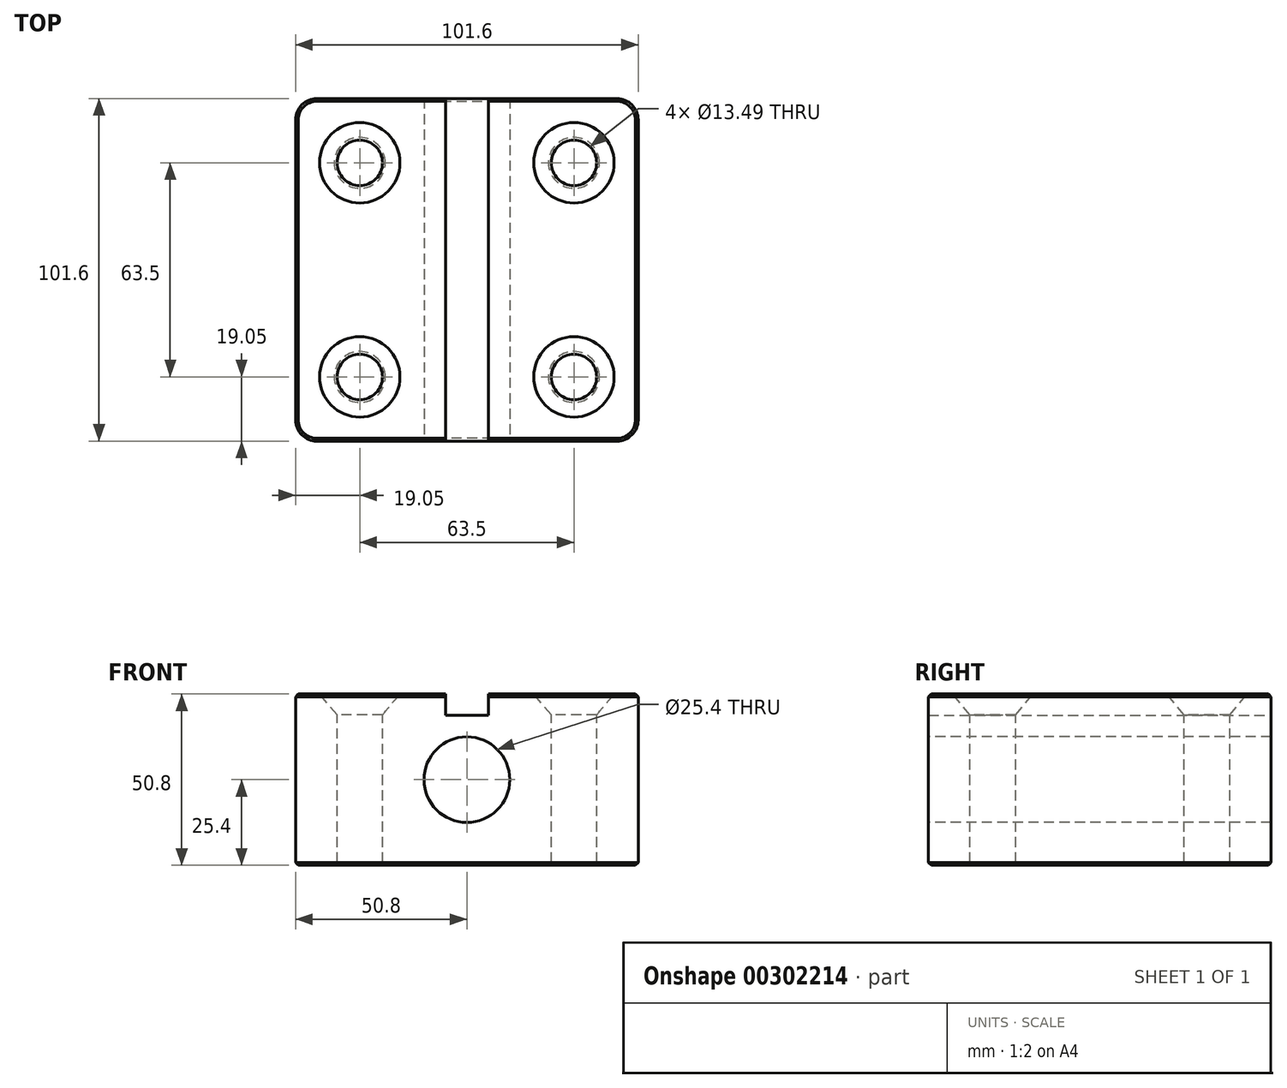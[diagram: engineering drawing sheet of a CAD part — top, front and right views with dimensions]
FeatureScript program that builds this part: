
annotation { "Feature Type Name" : "Feature", "Feature Type Description" : "" }
export const myFeature = defineFeature(function(context is Context, id is Id, definition is map)
    precondition{}
    {
        {
            var Q0;
            Q0=qCreatedBy(makeId("Front.planeOp"),FACE);
            var sketch = newSketch(context, id + "F0", { "sketchPlane" : qUnion([Q0])});
            skLineSegment(sketch, "E0.bottom", {"start": v(-50.8, 25.4) * mm, "end": v(-6.35, 25.4) * mm});
            skLineSegment(sketch, "E0.top", {"start": v(-50.8, -25.4) * mm, "end": v(50.8, -25.4) * mm});
            skLineSegment(sketch, "E0.left", {"start": v(-50.8, 25.4) * mm, "end": v(-50.8, -25.4) * mm});
            skLineSegment(sketch, "E0.right", {"start": v(50.8, 25.4) * mm, "end": v(50.8, -25.4) * mm});
            skLineSegment(sketch, "E1", {"start": v(-6.35, 25.4) * mm, "end": v(-6.35, 19.05) * mm});
            skLineSegment(sketch, "E2", {"start": v(6.35, 25.4) * mm, "end": v(6.35, 19.05) * mm});
            skLineSegment(sketch, "E3", {"start": v(-6.35, 19.05) * mm, "end": v(6.35, 19.05) * mm});
            skLineSegment(sketch, "E4.trimOffspring", {"start": v(6.35, 25.4) * mm, "end": v(50.8, 25.4) * mm});
            skSolve(sketch);
        }
        {
            var Q0;
            Q0=makeQuery(id+"F0.imprint","IMPRINT",FACE,{"disambiguationData":[TD([[makeQuery(id+"F0.imprint","IMPRINT",EDGE,{"derivedFrom":sQuery(id+"F0.wireOp",EDGE,"E0.bottom")}),-1.0]])]});
            extrude(context, id + "F1", {"entities" : qUnion([Q0]), "depth" : 50.8 * mm, "hasSecondDirection" : true, "secondDirectionOppositeDirection" : true, "secondDirectionDepth" : 50.8 * mm});
        }
        {
            var Q0;
            Q0=makeQuery(id+"F1.opExtrude","SWEPT_FACE",FACE,{"disambiguationData":[OSD([sQuery(id+"F0.wireOp",EDGE,"E0.bottom")])]});
            var sketch = newSketch(context, id + "F2", { "sketchPlane" : qUnion([Q0])});
            skPoint(sketch, "E5", {"position": v(-31.75, 31.75) * mm});
            skPoint(sketch, "E6.MirrorP", {"position": v(31.75, 31.75) * mm});
            skPoint(sketch, "E7.MirrorP", {"position": v(-31.75, -31.75) * mm});
            skPoint(sketch, "E8.MirrorP", {"position": v(31.75, -31.75) * mm});
            skSolve(sketch);
        }
        {
            var Q0;
            Q0=makeQuery(id+"F1.opExtrude","CAP_EDGE",EDGE,{"disambiguationData":[OSD([sQuery(id+"F0.wireOp",EDGE,"E0.left")])],"isStart":true});
            var Q1;
            Q1=makeQuery(id+"F1.opExtrude","CAP_EDGE",EDGE,{"disambiguationData":[OSD([sQuery(id+"F0.wireOp",EDGE,"E0.left")])],"isStart":false});
            var Q2;
            Q2=makeQuery(id+"F1.opExtrude","CAP_EDGE",EDGE,{"disambiguationData":[OSD([sQuery(id+"F0.wireOp",EDGE,"E0.right")])],"isStart":true});
            var Q3;
            Q3=makeQuery(id+"F1.opExtrude","CAP_EDGE",EDGE,{"disambiguationData":[OSD([sQuery(id+"F0.wireOp",EDGE,"E0.right")])],"isStart":false});
            fillet(context, id + "F3", {"entities" : qUnion([Q0, Q1, Q2, Q3]), "radius" : 6.35 * mm, "tangentPropagation" : true, "allowEdgeOverflow" : false});
        }
        {
            var Q0;
            Q0=sQuery(id+"F2.wireOp",VERTEX,"E5");
            var Q1;
            Q1=sQuery(id+"F2.wireOp",VERTEX,"E6.MirrorP");
            var Q2;
            Q2=sQuery(id+"F2.wireOp",VERTEX,"E7.MirrorP");
            var Q3;
            Q3=sQuery(id+"F2.wireOp",VERTEX,"E8.MirrorP");
            var Q4;
            Q4=makeQuery(id+"F1.opExtrude","SWEPT_BODY",BODY,{"disambiguationData":[OSD([sQuery(id+"F0.wireOp",EDGE,"E0.bottom"),sQuery(id+"F0.wireOp",EDGE,"E0.top"),sQuery(id+"F0.wireOp",EDGE,"E0.left"),sQuery(id+"F0.wireOp",EDGE,"E0.right")])]});
            hole(context, id + "F4", {"style" : HoleStyle.C_SINK, "endStyle" : HoleEndStyle.THROUGH, "holeDiameter" : 13.5 * mm, "cSinkDiameter" : 23.83 * mm, "cSinkAngle" : 80 * degree, "tappedDepth" : 12.7 * mm, "tapClearance" : 3, "locations" : qUnion([Q0, Q1, Q2, Q3]), "scope" : qUnion([Q4])});
        }
        {
            var Q0;
            Q0=makeQuery(id+"F1.opExtrude","SWEPT_EDGE",EDGE,{"disambiguationData":[OSD([sQuery(id+"F0.wireOp",EDGE,"E0.bottom"),sQuery(id+"F0.wireOp",EDGE,"E0.left")])]});
            var Q1;
            Q1=makeQuery(id+"F1.opExtrude","SWEPT_EDGE",EDGE,{"disambiguationData":[OSD([sQuery(id+"F0.wireOp",EDGE,"E0.top"),sQuery(id+"F0.wireOp",EDGE,"E0.right")])]});
            var Q2;
            Q2=makeQuery(id+"F1.opExtrude","SWEPT_EDGE",EDGE,{"disambiguationData":[OSD([sQuery(id+"F0.wireOp",EDGE,"E0.right"),sQuery(id+"F0.wireOp",EDGE,"E4.trimOffspring")])]});
            var Q3;
            Q3=makeQuery(id+"F1.opExtrude","SWEPT_FACE",FACE,{"disambiguationData":[OSD([sQuery(id+"F0.wireOp",EDGE,"E0.top")])]});
            var Q4;
            Q4=makeQuery(id+"F1.opExtrude","CAP_EDGE",EDGE,{"disambiguationData":[OSD([sQuery(id+"F0.wireOp",EDGE,"E0.bottom")])],"isStart":true});
            var Q5;
            Q5=makeQuery(id+"F1.opExtrude","SWEPT_EDGE",EDGE,{"disambiguationData":[OSD([sQuery(id+"F0.wireOp",EDGE,"E0.bottom"),sQuery(id+"F0.wireOp",EDGE,"E0.left")])]});
            var Q6;
            Q6=makeQuery(id+"F1.opExtrude","CAP_EDGE",EDGE,{"disambiguationData":[OSD([sQuery(id+"F0.wireOp",EDGE,"E0.bottom")])],"isStart":false});
            var Q7;
            Q7=makeQuery(id+"F1.opExtrude","CAP_EDGE",EDGE,{"disambiguationData":[OSD([sQuery(id+"F0.wireOp",EDGE,"E4.trimOffspring")])],"isStart":true});
            var Q8;
            Q8=makeQuery(id+"F1.opExtrude","CAP_EDGE",EDGE,{"disambiguationData":[OSD([sQuery(id+"F0.wireOp",EDGE,"E4.trimOffspring")])],"isStart":false});
            var Q9;
            Q9=makeQuery(id+"F3.opFillet","BLEND_EDGE",EDGE,{"blendedFrom":[makeQuery(id+"F1.opExtrude","CAP_EDGE",EDGE,{"disambiguationData":[OSD([sQuery(id+"F0.wireOp",EDGE,"E0.right")])],"isStart":false}),makeQuery(id+"F1.opExtrude","SWEPT_FACE",FACE,{"disambiguationData":[OSD([sQuery(id+"F0.wireOp",EDGE,"E4.trimOffspring")])]})],"blendedInto":[makeQuery(id+"F1.opExtrude","SWEPT_FACE",FACE,{"disambiguationData":[OSD([sQuery(id+"F0.wireOp",EDGE,"E4.trimOffspring")])]})]});
            var Q10;
            Q10=makeQuery(id+"F3.opFillet","BLEND_EDGE",EDGE,{"blendedFrom":[makeQuery(id+"F1.opExtrude","CAP_EDGE",EDGE,{"disambiguationData":[OSD([sQuery(id+"F0.wireOp",EDGE,"E0.right")])],"isStart":true}),makeQuery(id+"F1.opExtrude","SWEPT_FACE",FACE,{"disambiguationData":[OSD([sQuery(id+"F0.wireOp",EDGE,"E4.trimOffspring")])]})],"blendedInto":[makeQuery(id+"F1.opExtrude","SWEPT_FACE",FACE,{"disambiguationData":[OSD([sQuery(id+"F0.wireOp",EDGE,"E4.trimOffspring")])]})]});
            var Q11;
            Q11=makeQuery(id+"F3.opFillet","BLEND_EDGE",EDGE,{"blendedFrom":[makeQuery(id+"F1.opExtrude","CAP_EDGE",EDGE,{"disambiguationData":[OSD([sQuery(id+"F0.wireOp",EDGE,"E0.left")])],"isStart":true}),makeQuery(id+"F1.opExtrude","SWEPT_FACE",FACE,{"disambiguationData":[OSD([sQuery(id+"F0.wireOp",EDGE,"E0.bottom")])]})],"blendedInto":[makeQuery(id+"F1.opExtrude","SWEPT_FACE",FACE,{"disambiguationData":[OSD([sQuery(id+"F0.wireOp",EDGE,"E0.bottom")])]})]});
            var Q12;
            Q12=makeQuery(id+"F3.opFillet","BLEND_EDGE",EDGE,{"blendedFrom":[makeQuery(id+"F1.opExtrude","CAP_EDGE",EDGE,{"disambiguationData":[OSD([sQuery(id+"F0.wireOp",EDGE,"E0.left")])],"isStart":false}),makeQuery(id+"F1.opExtrude","SWEPT_FACE",FACE,{"disambiguationData":[OSD([sQuery(id+"F0.wireOp",EDGE,"E0.bottom")])]})],"blendedInto":[makeQuery(id+"F1.opExtrude","SWEPT_FACE",FACE,{"disambiguationData":[OSD([sQuery(id+"F0.wireOp",EDGE,"E0.bottom")])]})]});
            chamfer(context, id + "F5", {"entities" : qUnion([Q0, Q1, Q2, Q3, Q4, Q5, Q6, Q7, Q8, Q9, Q10, Q11, Q12]), "width" : 0.81 * mm, "tangentPropagation" : true});
        }
        {
            var Q0;
            Q0=makeQuery(id+"F1.opExtrude","CAP_FACE",FACE,{"disambiguationData":[OSD([sQuery(id+"F0.wireOp",EDGE,"E0.bottom"),sQuery(id+"F0.wireOp",EDGE,"E0.top"),sQuery(id+"F0.wireOp",EDGE,"E0.left"),sQuery(id+"F0.wireOp",EDGE,"E0.right"),sQuery(id+"F0.wireOp",EDGE,"E1"),sQuery(id+"F0.wireOp",EDGE,"E2"),sQuery(id+"F0.wireOp",EDGE,"E3"),sQuery(id+"F0.wireOp",EDGE,"E4.trimOffspring")])],"isStart":false});
            var sketch = newSketch(context, id + "F6", { "sketchPlane" : qUnion([Q0])});
            skPoint(sketch, "E9", {"position": v(0, 0) * mm});
            skSolve(sketch);
        }
        {
            var Q0;
            Q0=sQuery(id+"F6.wireOp",VERTEX,"E9");
            var Q1;
            Q1=makeQuery(id+"F1.opExtrude","SWEPT_BODY",BODY,{"disambiguationData":[OSD([sQuery(id+"F0.wireOp",EDGE,"E0.bottom"),sQuery(id+"F0.wireOp",EDGE,"E0.top"),sQuery(id+"F0.wireOp",EDGE,"E0.left"),sQuery(id+"F0.wireOp",EDGE,"E0.right"),sQuery(id+"F0.wireOp",EDGE,"E1"),sQuery(id+"F0.wireOp",EDGE,"E2"),sQuery(id+"F0.wireOp",EDGE,"E3"),sQuery(id+"F0.wireOp",EDGE,"E4.trimOffspring")])]});
            hole(context, id + "F7", {"style" : HoleStyle.SIMPLE, "endStyle" : HoleEndStyle.THROUGH, "holeDiameter" : 25.4 * mm, "tappedDepth" : 12.7 * mm, "tapClearance" : 3, "locations" : qUnion([Q0]), "scope" : qUnion([Q1])});
        }
    });
